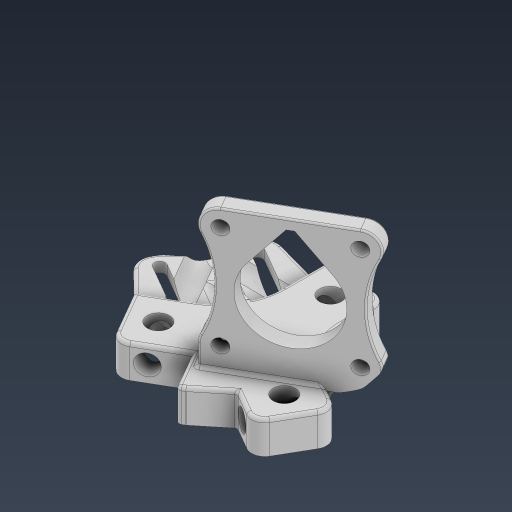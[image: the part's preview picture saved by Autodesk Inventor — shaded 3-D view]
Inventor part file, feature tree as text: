
AUTODESK INVENTOR PART (.ipt)
format: ipt  version: 2024 (Build 280153000, 153)  size: 910,336 bytes
history: native  units: mm
features: sketch x17, extrude x15, fillet x9, chamfer x6, hole x4, projected_geometry x4, plane x3, pattern_circular x2, mirror x1
ambient origin geometry x8: Origin, YZ Plane, XZ Plane, XY Plane, X Axis, Y Axis, Z Axis, Center Point
bodies: Solid1 (feature_tree)
feature tree (61):
  sketch  "Sketch1"  dims[d0=22.0mm d1=12.0mm]
  extrude  "Extrusion1"  Depth=22.0mm
  hole  "Hole1"  [1 undecoded]
  sketch  "Sketch2"  dims[d2=10.0mm d3=0.0mm]
  plane  "Work Plane1"
  plane  "Work Plane2"
  plane  "Work Plane3"
  sketch  "Sketch3"  dims[d4=6.65mm d5=6.0mm d6=4.0mm d7=2.0mm d8=90.0deg d9=8.0mm d10=20.594885mm d11=90.0deg]
  extrude  "Extrusion3"  TaperAngle=90.0deg  [1 undecoded]
  pattern_circular  "Circular Pattern2"  Count=3 Angle=360.0deg
  extrude  "Extrusion4"  Depth=3.0mm TaperAngle=0.0deg
  extrude  "Extrusion5"  TaperAngle=0.0deg  [1 undecoded]
  pattern_circular  "Circular Pattern4"  Count=3 Angle=360.0deg
  hole  "Hole2"  [1 undecoded]
  mirror  "Mirror1"
  sketch  "Sketch13"  dims[d16=3.325mm]
  extrude  "Extrusion7"  TaperAngle=90.0deg  [1 undecoded]
  extrude  "Extrusion8"  Depth=2.0mm
  extrude  "Extrusion10"  Depth=10.0mm
  hole  "Hole4"  [1 undecoded]
  extrude  "Extrusion11"  Depth=10.0mm TaperAngle=0.0deg
  hole  "Hole5"  [1 undecoded]
  sketch  "Sketch23"  dims[d44=5.1mm d45=0.0mm d46=0.0mm d50=30.0mm d51=360.0deg]
  extrude  "Extrusion12"  Depth=10.0mm TaperAngle=0.0deg
  extrude  "Extrusion14"  Depth=10.0mm
  extrude  "Extrusion15"  Depth=10.0mm TaperAngle=0.0deg
  extrude  "Extrusion16"  Depth=10.0mm
  chamfer  "Chamfer1"  Distance=6.5mm
  fillet  "Fillet8"  Radius=5.0mm
  extrude  "Extrusion17"  Depth=10.0mm
  extrude  "Extrusion18"  Depth=10.0mm
  fillet  "Fillet9"  Radius=31.0mm
  chamfer  "Chamfer2"  Distance=31.0mm
  extrude  "Extrusion20"  Depth=10.0mm
  chamfer  "Chamfer6"  Distance=30.0mm
  chamfer  "Chamfer7"  Distance=30.0mm
  fillet  "Fillet15"  Radius=5.0mm
  fillet  "Fillet16"  Radius=8.0mm
  fillet  "Fillet18"  [1 undecoded]
  fillet  "Fillet20"  [1 undecoded]
  fillet  "Fillet21"  Radius=8.726646mm
  fillet  "Fillet22"  Radius=10.0mm
  fillet  "Fillet23"  Radius=3.4mm
  chamfer  "Chamfer8"  Distance=5.0mm
  chamfer  "Chamfer9"  Distance=2.0mm
  sketch  "Sketch4"  dims[d12=90.0deg d13=90.0deg]
  sketch  "Sketch6"  dims[d14=6.2mm]
  sketch  "Sketch9"  dims[d15=5.0mm]
  sketch  "Sketch18"  dims[d17=6.65mm]
  projected_geometry  "Projected Loop3"
  sketch  "Sketch19"  dims[d23=6.0mm]
  sketch  "Sketch20"  dims[d25=10.0mm d26=0.0mm d27=30.0mm d28=360.0deg]
  sketch  "Sketch22"  dims[d30=17.0mm d31=28.0mm d32=30.94mm d33=4.372mm d34=18.4mm d35=4.662mm d36=4.662mm d37=3.23mm d38=3.23mm d39=6.5mm d40=6.5mm d42=3.0mm d43=0.0mm]
  projected_geometry  "Projected Loop4"
  sketch  "Sketch24"  dims[d55=8.0mm d56=6.0mm d57=4.0mm d58=2.0mm d59=90.0deg d60=8.0mm d61=20.594885mm d62=19.365844mm]
  sketch  "Sketch25"  dims[d63=19.365844mm d83=90.0deg]
  sketch  "Sketch26"  dims[d84=2.0mm d85=2.0mm]
  sketch  "Sketch27"  dims[d86=10.0mm d87=12.9mm]
  projected_geometry  "Projected Loop5"
  projected_geometry  "Projected Loop6"
  sketch  "Sketch30"  dims[d88=7.0mm d90=9.15mm d91=10.0mm d92=0.0mm d93=0.0mm d94=0.0mm d113=1.0mm d114=0.0mm d115=5.0mm d116=9.0mm d118=41.0mm d121=42.5mm d122=0.0mm d124=2.0mm d125=6.0mm d126=4.0mm d127=2.0mm d128=90.0deg d129=9.394mm d130=0.0mm d131=3.1mm d132=6.5mm d133=5.0mm d134=2.5mm d153=4.2mm d154=6.0mm d155=8.0mm d156=4.0mm d157=90.0deg d158=9.394mm d159=0.0mm d160=5.0mm d161=31.0mm d162=31.0mm d163=5.0mm d164=30.0mm d166=30.0mm d168=5.0mm d169=0.0mm d173=8.0mm d174=0.0mm d175=0.0mm d176=0.0mm d177=0.0mm d178=8.726646mm d179=10.0mm d180=0.0mm d183=3.4mm d184=2.0mm d185=45.0deg d187=5.0mm d188=2.0mm d189=0.0mm d191=25.0mm d192=8.726646mm d193=8.726646mm d194=0.0mm d195=0.0mm d196=0.5mm d197=1.5mm d198=2.0mm d199=45.0deg d216=4.0mm d217=0.0mm d218=6.601mm d219=25.3mm d220=4.537856mm d221=6.601mm d222=25.3mm d223=4.537856mm d224=5.0mm d225=2.0mm d227=2.0mm d229=1.0mm d230=1.0mm d231=1.0mm d232=4.0mm d233=0.2mm d234=25.3mm d235=4.537856mm d236=0.5mm d237=25.3mm d238=4.537856mm d212=0.0mm d213=0.0mm d214=0.0mm d215=0.0mm]
note: 9 required parameter values undecoded (feature->parameter linkage not recoverable at this tier; creation-order binding heuristic only, values carry confidence <= 0.55)
